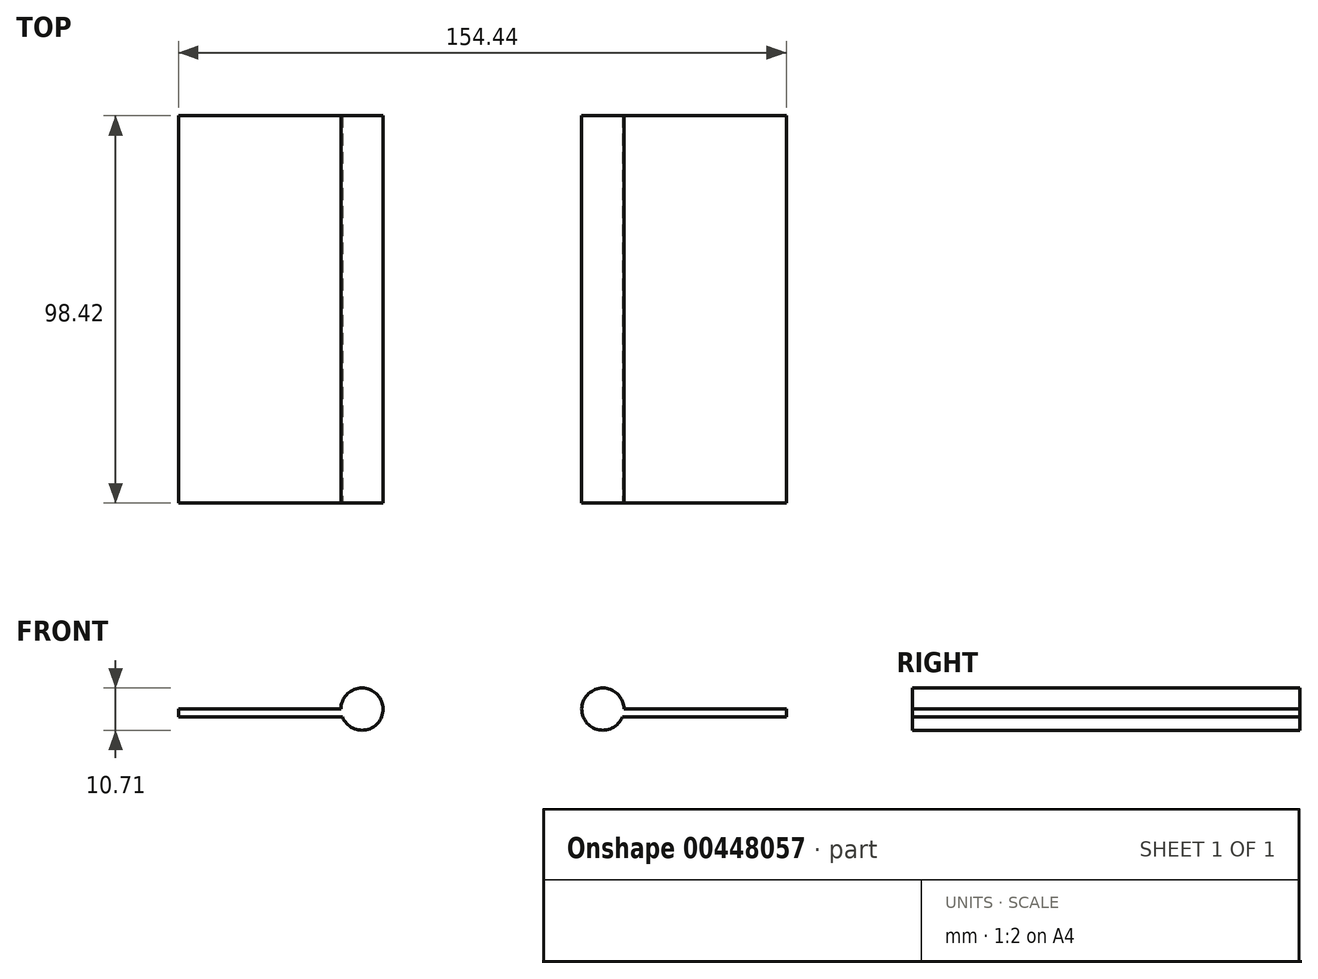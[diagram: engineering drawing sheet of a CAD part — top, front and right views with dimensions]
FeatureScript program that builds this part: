
annotation { "Feature Type Name" : "Feature", "Feature Type Description" : "" }
export const myFeature = defineFeature(function(context is Context, id is Id, definition is map)
    precondition{}
    {
        {
            var Q0;
            Q0=qCreatedBy(makeId("Top.planeOp"),FACE);
            var sketch = newSketch(context, id + "F0", { "sketchPlane" : qUnion([Q0])});
            skLineSegment(sketch, "E0.bottom", {"start": v(-77.22, 49.21) * mm, "end": v(-35.95, 49.21) * mm});
            skLineSegment(sketch, "E0.top", {"start": v(-77.22, -49.21) * mm, "end": v(-35.95, -49.21) * mm});
            skLineSegment(sketch, "E0.left", {"start": v(-77.22, 49.21) * mm, "end": v(-77.22, -49.21) * mm});
            skLineSegment(sketch, "E0.right", {"start": v(-35.95, 49.21) * mm, "end": v(-35.95, -49.21) * mm});
            skPoint(sketch, "E0.middle", {"position": v(-56.59, 0) * mm});
            skLineSegment(sketch, "E1.MirrorCS", {"start": v(77.22, 49.21) * mm, "end": v(35.95, 49.21) * mm});
            skPoint(sketch, "E2.MirrorP", {"position": v(56.59, 0) * mm});
            skLineSegment(sketch, "E3.MirrorCS", {"start": v(35.95, 49.21) * mm, "end": v(35.95, -49.21) * mm});
            skLineSegment(sketch, "E4.MirrorCS", {"start": v(77.22, 49.21) * mm, "end": v(77.22, -49.21) * mm});
            skLineSegment(sketch, "E5.MirrorCS", {"start": v(77.22, -49.21) * mm, "end": v(35.95, -49.21) * mm});
            skSolve(sketch);
        }
        {
            var Q0;
            Q0 = qSketchRegion(id + "F0", true);
            extrude(context, id + "F1", {"entities" : qUnion([Q0]), "depth" : 1.98 * mm});
        }
        {
            var Q0;
            Q0=makeQuery(id+"F1.opExtrude","SWEPT_FACE",FACE,{"disambiguationData":[OSD([sQuery(id+"F0.wireOp",EDGE,"E0.top")])]});
            var sketch = newSketch(context, id + "F2", { "sketchPlane" : qUnion([Q0])});
            skLineSegment(sketch, "E6", {"start": v(-35.95, 1.98) * mm, "end": v(-30.6, 1.98) * mm});
            skCircle(sketch, "E7", {"center": v(-30.6, 1.98) * mm, "radius": 5.36 * mm});
            skLineSegment(sketch, "E8", {"start": v(-35.95, 0) * mm, "end": v(-35.57, 0) * mm});
            skSolve(sketch);
        }
        {
            var Q0;
            {var subQ3=sQuery(id+"F2.wireOp",EDGE,"E8");Q0=makeQuery(id+"F2.imprint","IMPRINT",FACE,{"disambiguationData":[TD([[makeQuery(id+"F2.imprint","IMPRINT",EDGE,{"derivedFrom":subQ3}),1.0]])]});}
            var Q1;
            {var subQ0=sQuery(id+"F2.wireOp",EDGE,"E7");var subQ3=makeQuery(id+"F2.imprint","INTERSECT",VERTEX,{"derivedFrom":[subQ0,sQuery(id+"F2.wireOp",EDGE,"E8")]});Q1=makeQuery(id+"F2.imprint","IMPRINT",FACE,{"disambiguationData":[TD([[makeQuery(id+"F2.imprint","IMPRINT",EDGE,{"disambiguationData":[TD([[subQ3,1.0]])],"derivedFrom":subQ0}),1.0]])]});}
            extrude(context, id + "F3", {"entities" : qUnion([Q0, Q1]), "operationType" : NewBodyOperationType.ADD, "oppositeDirection" : true, "depth" : 98.42 * mm});
        }
        {
            var Q0;
            Q0=makeQuery(id+"F1.opExtrude","SWEPT_BODY",BODY,{"disambiguationData":[OSD([sQuery(id+"F0.wireOp",EDGE,"E0.bottom"),sQuery(id+"F0.wireOp",EDGE,"E0.top"),sQuery(id+"F0.wireOp",EDGE,"E0.left"),sQuery(id+"F0.wireOp",EDGE,"E0.right")])]});
            var Q1;
            Q1=qCreatedBy(makeId("Right.planeOp"),FACE);
            mirror(context, id + "F4", {"operationType" : NewBodyOperationType.ADD, "entities" : qUnion([Q0]), "mirrorPlane" : qUnion([Q1])});
        }
    });
